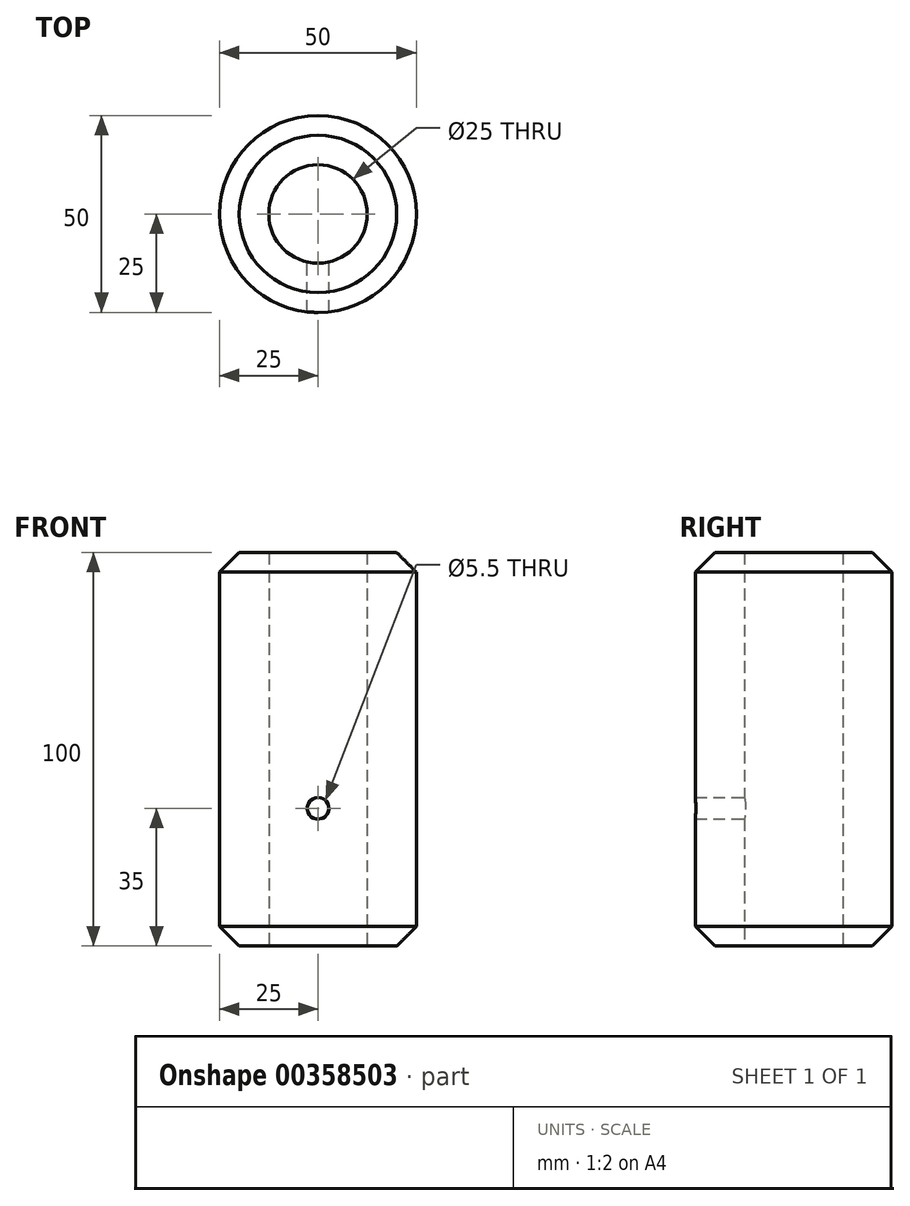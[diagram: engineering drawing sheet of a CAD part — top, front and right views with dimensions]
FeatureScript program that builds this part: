
annotation { "Feature Type Name" : "Feature", "Feature Type Description" : "" }
export const myFeature = defineFeature(function(context is Context, id is Id, definition is map)
    precondition{}
    {
        {
            var Q0;
            Q0=qCreatedBy(makeId("Top.planeOp"),FACE);
            var sketch = newSketch(context, id + "F0", { "sketchPlane" : qUnion([Q0])});
            skCircle(sketch, "E0", {"center": v(0, 0) * mm, "radius": 25 * mm});
            skCircle(sketch, "E1", {"center": v(0, 0) * mm, "radius": 12.5 * mm});
            skSolve(sketch);
        }
        {
            var Q0;
            Q0=makeQuery(id+"F0.imprint","IMPRINT",FACE,{"disambiguationData":[TD([[makeQuery(id+"F0.imprint","IMPRINT",EDGE,{"derivedFrom":sQuery(id+"F0.wireOp",EDGE,"E0")}),1.0]])]});
            extrude(context, id + "F1", {"entities" : qUnion([Q0]), "depth" : 100 * mm});
        }
        {
            var Q0;
            Q0=makeQuery(id+"F1.opExtrude","CAP_EDGE",EDGE,{"disambiguationData":[OSD([sQuery(id+"F0.wireOp",EDGE,"E0")])],"isStart":false});
            chamfer(context, id + "F2", {"entities" : qUnion([Q0]), "width" : 5 * mm, "tangentPropagation" : true});
        }
        {
            var Q0;
            Q0=makeQuery(id+"F1.opExtrude","CAP_EDGE",EDGE,{"disambiguationData":[OSD([sQuery(id+"F0.wireOp",EDGE,"E0")])],"isStart":true});
            chamfer(context, id + "F3", {"entities" : qUnion([Q0]), "width" : 5 * mm, "tangentPropagation" : true});
        }
        {
            var Q0;
            Q0=qCreatedBy(makeId("Front.planeOp"),FACE);
            var sketch = newSketch(context, id + "F4", { "sketchPlane" : qUnion([Q0])});
            skCircle(sketch, "E2", {"center": v(0, 35) * mm, "radius": 2.5 * mm});
            skSolve(sketch);
        }
        {
            var Q0;
            Q0=sQuery(id+"F4.wireOp",VERTEX,"E2.center");
            var Q1;
            Q1=makeQuery(id+"F1.opExtrude","SWEPT_BODY",BODY,{"disambiguationData":[OSD([sQuery(id+"F0.wireOp",EDGE,"E0"),sQuery(id+"F0.wireOp",EDGE,"E1")])]});
            hole(context, id + "F5", {"style" : HoleStyle.SIMPLE, "endStyle" : HoleEndStyle.THROUGH, "oppositeDirection" : true, "standardTappedOrClearance" : lookupTablePath({ "fit" : "Normal", "standard" : "ISO", "size" : "M5", "type" : "Clearance" }), "standardBlindInLast" : lookupTablePath({ "fit" : "Standard", "standard" : "ISO", "size" : "M5", "type" : "Clearance" }), "holeDiameter" : 5.5 * mm, "isTappedThrough" : true, "tappedDepth" : 12 * mm, "tapClearance" : 3, "locations" : qUnion([Q0]), "scope" : qUnion([Q1])});
        }
    });
